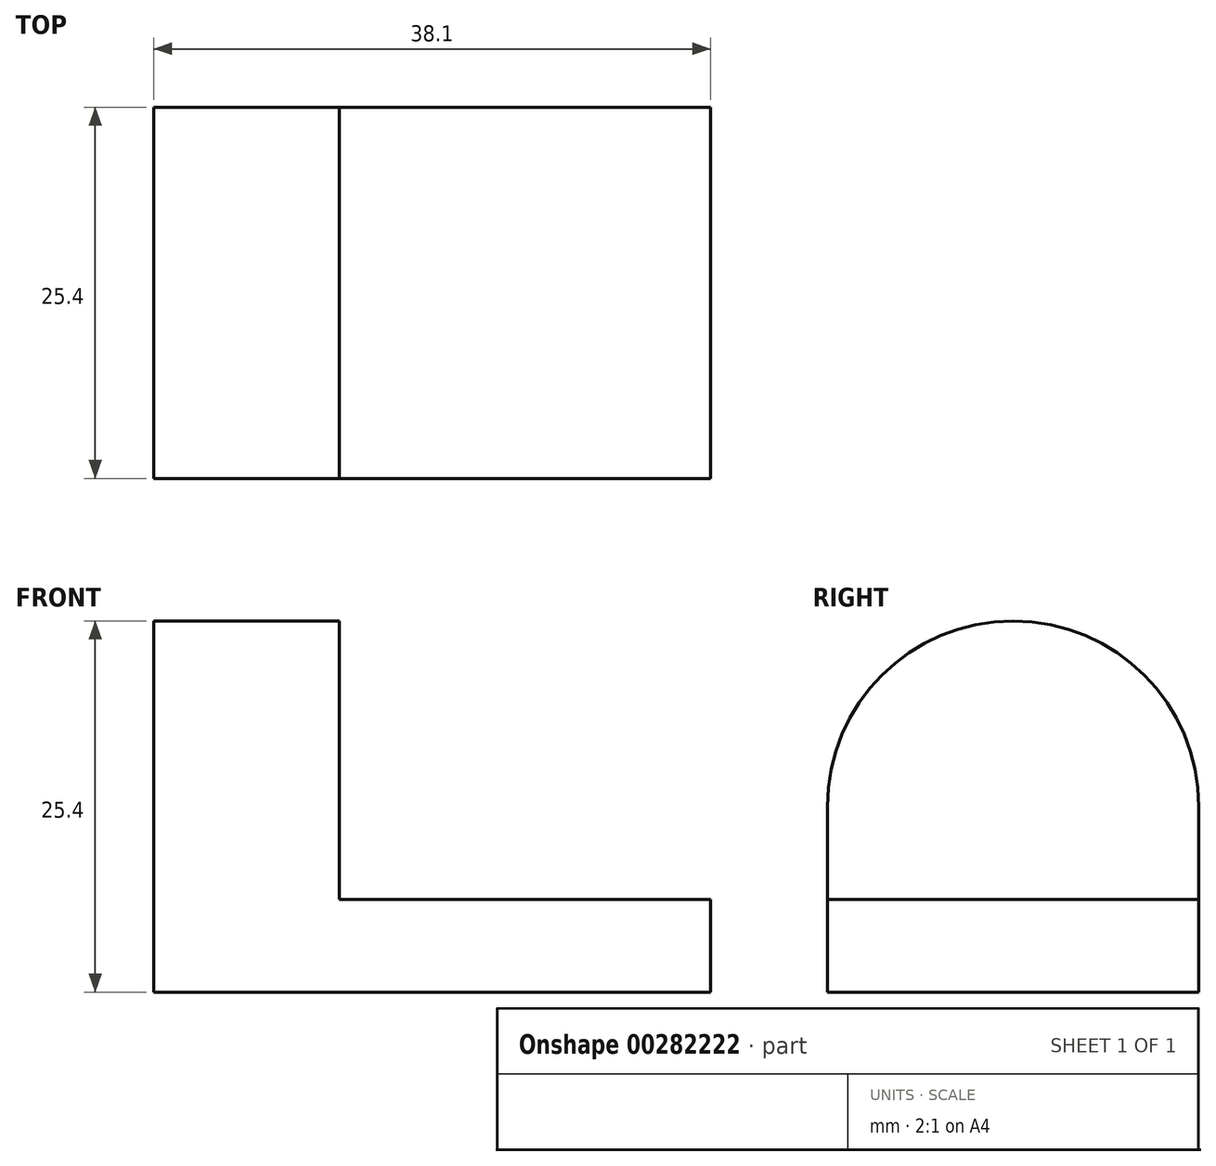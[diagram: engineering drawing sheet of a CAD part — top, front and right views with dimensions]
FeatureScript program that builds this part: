
annotation { "Feature Type Name" : "Feature", "Feature Type Description" : "" }
export const myFeature = defineFeature(function(context is Context, id is Id, definition is map)
    precondition{}
    {
        {
            var Q0;
            Q0=qCreatedBy(makeId("Right.planeOp"),FACE);
            var sketch = newSketch(context, id + "F0", { "sketchPlane" : qUnion([Q0])});
            skLineSegment(sketch, "E0", {"start": v(-12.7, 0) * mm, "end": v(-12.7, 12.7) * mm});
            skLineSegment(sketch, "E1", {"start": v(-12.7, 0) * mm, "end": v(12.7, 0) * mm});
            skLineSegment(sketch, "E2", {"start": v(12.7, 0) * mm, "end": v(12.7, 12.7) * mm});
            skArc(sketch, "E3", {"start": v(12.7, 12.7) * mm, "mid": v(0, 25.4) * mm, "end": v(-12.7, 12.7) * mm});
            skSolve(sketch);
        }
        {
            var Q0;
            Q0=makeQuery(id+"F0.imprint","IMPRINT",FACE,{"disambiguationData":[TD([[makeQuery(id+"F0.imprint","IMPRINT",EDGE,{"derivedFrom":sQuery(id+"F0.wireOp",EDGE,"E0")}),-1.0]])]});
            extrude(context, id + "F1", {"entities" : qUnion([Q0]), "depth" : 12.7 * mm});
        }
        {
            var Q0;
            Q0=makeQuery(id+"F1.opExtrude","CAP_FACE",FACE,{"disambiguationData":[OSD([sQuery(id+"F0.wireOp",EDGE,"E0"),sQuery(id+"F0.wireOp",EDGE,"E1"),sQuery(id+"F0.wireOp",EDGE,"E2"),sQuery(id+"F0.wireOp",EDGE,"E3")])],"isStart":false});
            var sketch = newSketch(context, id + "F2", { "sketchPlane" : qUnion([Q0])});
            skLineSegment(sketch, "E4", {"start": v(-12.7, 6.35) * mm, "end": v(12.7, 6.35) * mm});
            skLineSegment(sketch, "E5", {"start": v(-12.7, 6.35) * mm, "end": v(-12.7, 0) * mm});
            skLineSegment(sketch, "E6", {"start": v(-12.7, 0) * mm, "end": v(12.7, 0) * mm});
            skLineSegment(sketch, "E7", {"start": v(12.7, 0) * mm, "end": v(12.7, 6.35) * mm});
            skSolve(sketch);
        }
        {
            var Q0;
            Q0=makeQuery(id+"F2.imprint","IMPRINT",FACE,{"disambiguationData":[TD([[makeQuery(id+"F2.imprint","IMPRINT",EDGE,{"derivedFrom":sQuery(id+"F2.wireOp",EDGE,"E4")}),-1.0]])]});
            extrude(context, id + "F3", {"entities" : qUnion([Q0]), "operationType" : NewBodyOperationType.ADD, "depth" : 25.4 * mm});
        }
    });
